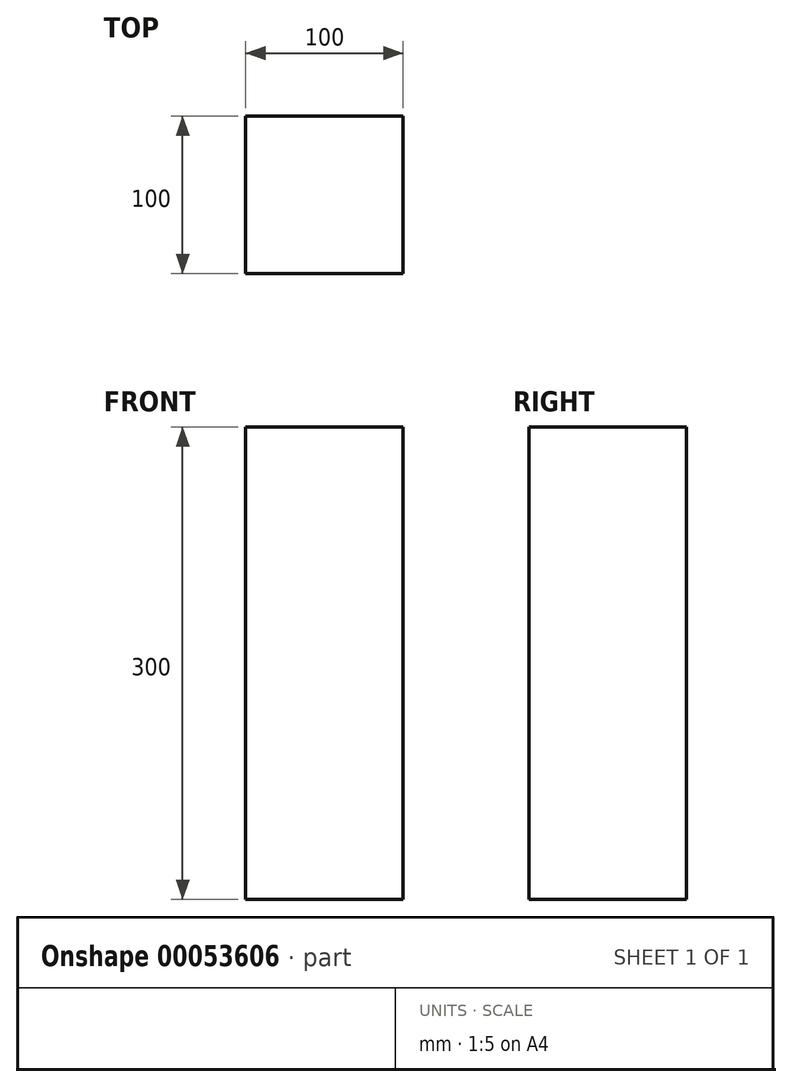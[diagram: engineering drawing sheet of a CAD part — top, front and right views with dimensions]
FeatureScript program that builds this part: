
annotation { "Feature Type Name" : "Feature", "Feature Type Description" : "" }
export const myFeature = defineFeature(function(context is Context, id is Id, definition is map)
    precondition{}
    {
        {
            var Q0;
            Q0=qCreatedBy(makeId("Top.planeOp"),FACE);
            var sketch = newSketch(context, id + "F0", { "sketchPlane" : qUnion([Q0])});
            skLineSegment(sketch, "E0.bottom", {"start": v(-57.3, 49.47) * mm, "end": v(42.7, 49.47) * mm});
            skLineSegment(sketch, "E0.top", {"start": v(-57.3, -50.53) * mm, "end": v(42.7, -50.53) * mm});
            skLineSegment(sketch, "E0.left", {"start": v(-57.3, 49.47) * mm, "end": v(-57.3, -50.53) * mm});
            skLineSegment(sketch, "E0.right", {"start": v(42.7, 49.47) * mm, "end": v(42.7, -50.53) * mm});
            skSolve(sketch);
        }
        {
            var Q0;
            Q0 = qSketchRegion(id + "F0", true);
            extrude(context, id + "F1", {"entities" : qUnion([Q0]), "depth" : 300 * mm});
        }
    });
